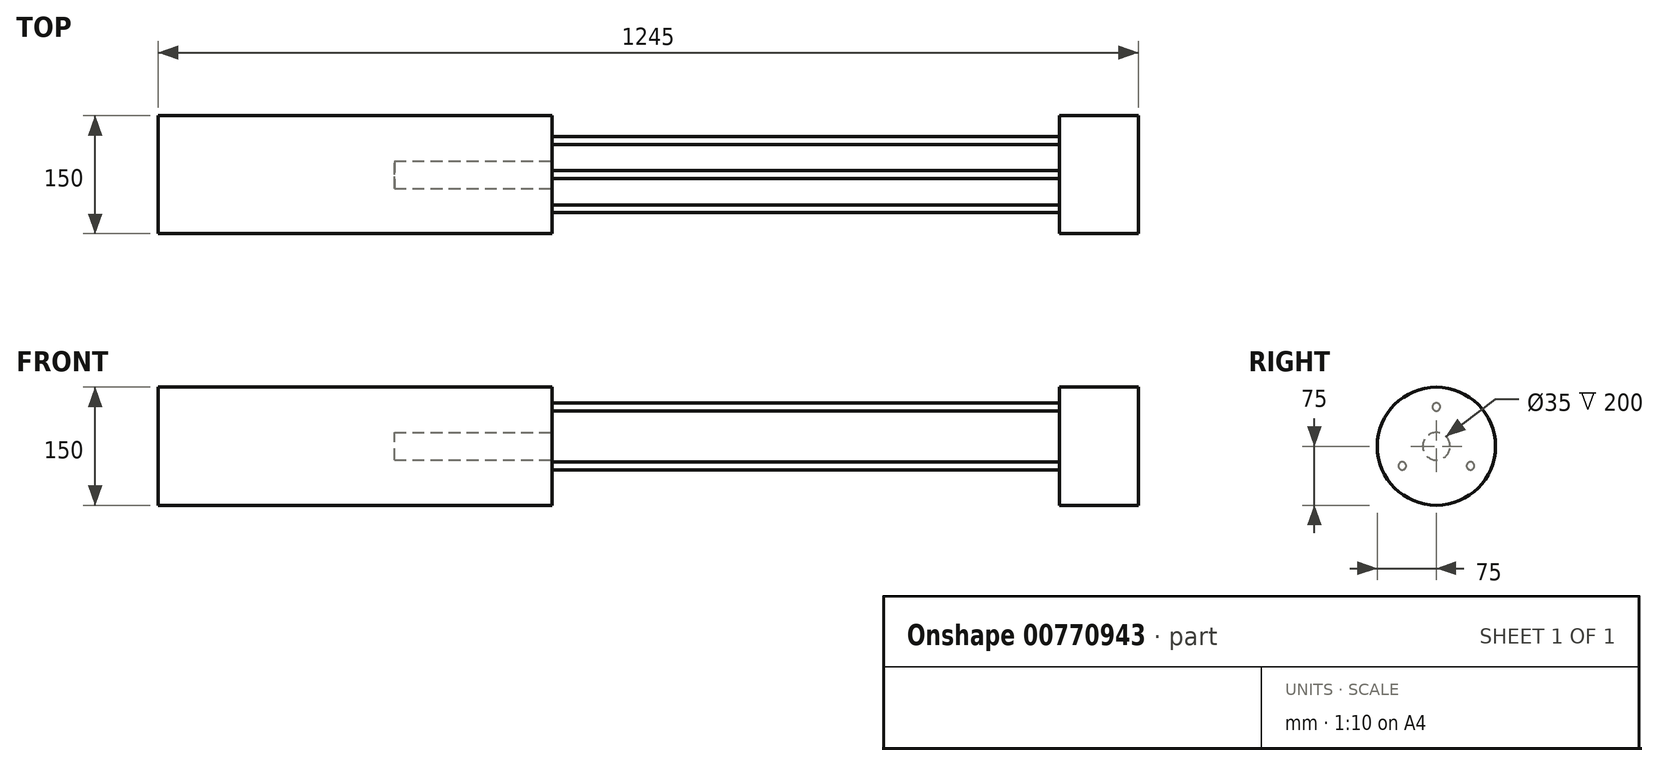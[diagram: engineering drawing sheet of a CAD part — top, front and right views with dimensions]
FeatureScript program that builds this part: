
annotation { "Feature Type Name" : "Feature", "Feature Type Description" : "" }
export const myFeature = defineFeature(function(context is Context, id is Id, definition is map)
    precondition{}
    {
        {
            var Q0;
            Q0=qCreatedBy(makeId("Top.planeOp"),FACE);
            var sketch = newSketch(context, id + "F0", { "sketchPlane" : qUnion([Q0])});
            skLineSegment(sketch, "E0", {"start": v(-500, 0) * mm, "end": v(-500, -75) * mm});
            skLineSegment(sketch, "E1", {"start": v(-500, -75) * mm, "end": v(0, -75) * mm});
            skLineSegment(sketch, "E2", {"start": v(0, -75) * mm, "end": v(0, -17.5) * mm});
            skLineSegment(sketch, "E3", {"start": v(0, -17.5) * mm, "end": v(-200, -17.5) * mm});
            skLineSegment(sketch, "E4", {"start": v(-200, -17.5) * mm, "end": v(-200, 0) * mm});
            skLineSegment(sketch, "E5", {"start": v(-200, 0) * mm, "end": v(-500, 0) * mm});
            skSolve(sketch);
        }
        {
            var Q0;
            Q0=qCreatedBy(makeId("Top.planeOp"),FACE);
            var sketch = newSketch(context, id + "F1", { "sketchPlane" : qUnion([Q0])});
            skLineSegment(sketch, "E6.bottom", {"start": v(645, -75) * mm, "end": v(745, -75) * mm});
            skLineSegment(sketch, "E6.top", {"start": v(645, 0) * mm, "end": v(745, 0) * mm});
            skLineSegment(sketch, "E6.left", {"start": v(645, -75) * mm, "end": v(645, 0) * mm});
            skLineSegment(sketch, "E6.right", {"start": v(745, -75) * mm, "end": v(745, 0) * mm});
            skSolve(sketch);
        }
        {
            var Q0;
            Q0=makeQuery(id+"F0.imprint","IMPRINT",FACE,{"disambiguationData":[TD([[makeQuery(id+"F0.imprint","IMPRINT",EDGE,{"derivedFrom":sQuery(id+"F0.wireOp",EDGE,"E0")}),1.0]])]});
            var Q1;
            Q1=makeQuery(id+"FkN8uBkjpyCZk5b_23.imprint","IMPRINT",FACE,{"disambiguationData":[TD([[makeQuery(id+"FkN8uBkjpyCZk5b_23.imprint","IMPRINT",EDGE,{"derivedFrom":sQuery(id+"FkN8uBkjpyCZk5b_23.wireOp",EDGE,"00949d21-04e9-4acd-8803-175544acd0f4.4.0.0")}),1.0]])]});
            var Q2;
            Q2=makeQuery(id+"FkN8uBkjpyCZk5b_23.imprint","IMPRINT",FACE,{"disambiguationData":[TD([[makeQuery(id+"FkN8uBkjpyCZk5b_23.imprint","IMPRINT",EDGE,{"derivedFrom":sQuery(id+"FkN8uBkjpyCZk5b_23.wireOp",EDGE,"00949d21-04e9-4acd-8803-175544acd0f4.9.0.0")}),1.0]])]});
            var Q3;
            Q3=makeQuery(id+"FkN8uBkjpyCZk5b_23.imprint","IMPRINT",FACE,{"disambiguationData":[TD([[makeQuery(id+"FkN8uBkjpyCZk5b_23.imprint","IMPRINT",EDGE,{"derivedFrom":sQuery(id+"FkN8uBkjpyCZk5b_23.wireOp",EDGE,"00949d21-04e9-4acd-8803-175544acd0f4.3.0.0")}),1.0]])]});
            var Q4;
            Q4=makeQuery(id+"FkN8uBkjpyCZk5b_23.imprint","IMPRINT",FACE,{"disambiguationData":[TD([[makeQuery(id+"FkN8uBkjpyCZk5b_23.imprint","IMPRINT",EDGE,{"derivedFrom":sQuery(id+"FkN8uBkjpyCZk5b_23.wireOp",EDGE,"00949d21-04e9-4acd-8803-175544acd0f4.2.0.0")}),1.0]])]});
            var Q5;
            Q5=makeQuery(id+"FkN8uBkjpyCZk5b_23.imprint","IMPRINT",FACE,{"disambiguationData":[TD([[makeQuery(id+"FkN8uBkjpyCZk5b_23.imprint","IMPRINT",EDGE,{"derivedFrom":sQuery(id+"FkN8uBkjpyCZk5b_23.wireOp",EDGE,"00949d21-04e9-4acd-8803-175544acd0f4.10.0.0")}),1.0]])]});
            var Q6;
            Q6=makeQuery(id+"FkN8uBkjpyCZk5b_23.imprint","IMPRINT",FACE,{"disambiguationData":[TD([[makeQuery(id+"FkN8uBkjpyCZk5b_23.imprint","IMPRINT",EDGE,{"derivedFrom":sQuery(id+"FkN8uBkjpyCZk5b_23.wireOp",EDGE,"00949d21-04e9-4acd-8803-175544acd0f4.1.0.0")}),1.0]])]});
            var Q7;
            Q7=makeQuery(id+"FkN8uBkjpyCZk5b_23.imprint","IMPRINT",FACE,{"disambiguationData":[TD([[makeQuery(id+"FkN8uBkjpyCZk5b_23.imprint","IMPRINT",EDGE,{"derivedFrom":sQuery(id+"FkN8uBkjpyCZk5b_23.wireOp",EDGE,"00949d21-04e9-4acd-8803-175544acd0f4.8.0.0")}),1.0]])]});
            var Q8;
            Q8=makeQuery(id+"FkN8uBkjpyCZk5b_23.imprint","IMPRINT",FACE,{"disambiguationData":[TD([[makeQuery(id+"FkN8uBkjpyCZk5b_23.imprint","IMPRINT",EDGE,{"derivedFrom":sQuery(id+"FkN8uBkjpyCZk5b_23.wireOp",EDGE,"00949d21-04e9-4acd-8803-175544acd0f4.17.0.0")}),1.0]])]});
            var Q9;
            Q9=makeQuery(id+"FkN8uBkjpyCZk5b_23.imprint","IMPRINT",FACE,{"disambiguationData":[TD([[makeQuery(id+"FkN8uBkjpyCZk5b_23.imprint","IMPRINT",EDGE,{"derivedFrom":sQuery(id+"FkN8uBkjpyCZk5b_23.wireOp",EDGE,"00949d21-04e9-4acd-8803-175544acd0f4.16.0.0")}),1.0]])]});
            var Q10;
            Q10=makeQuery(id+"FkN8uBkjpyCZk5b_23.imprint","IMPRINT",FACE,{"disambiguationData":[TD([[makeQuery(id+"FkN8uBkjpyCZk5b_23.imprint","IMPRINT",EDGE,{"derivedFrom":sQuery(id+"FkN8uBkjpyCZk5b_23.wireOp",EDGE,"00949d21-04e9-4acd-8803-175544acd0f4.12.0.0")}),1.0]])]});
            var Q11;
            Q11=makeQuery(id+"FkN8uBkjpyCZk5b_23.imprint","IMPRINT",FACE,{"disambiguationData":[TD([[makeQuery(id+"FkN8uBkjpyCZk5b_23.imprint","IMPRINT",EDGE,{"derivedFrom":sQuery(id+"FkN8uBkjpyCZk5b_23.wireOp",EDGE,"00949d21-04e9-4acd-8803-175544acd0f4.5.0.0")}),1.0]])]});
            var Q12;
            Q12=makeQuery(id+"FkN8uBkjpyCZk5b_23.imprint","IMPRINT",FACE,{"disambiguationData":[TD([[makeQuery(id+"FkN8uBkjpyCZk5b_23.imprint","IMPRINT",EDGE,{"derivedFrom":sQuery(id+"FkN8uBkjpyCZk5b_23.wireOp",EDGE,"00949d21-04e9-4acd-8803-175544acd0f4.6.0.0")}),1.0]])]});
            var Q13;
            Q13=makeQuery(id+"FkN8uBkjpyCZk5b_23.imprint","IMPRINT",FACE,{"disambiguationData":[TD([[makeQuery(id+"FkN8uBkjpyCZk5b_23.imprint","IMPRINT",EDGE,{"derivedFrom":sQuery(id+"FkN8uBkjpyCZk5b_23.wireOp",EDGE,"00949d21-04e9-4acd-8803-175544acd0f4.11.0.0")}),1.0]])]});
            var Q14;
            Q14=makeQuery(id+"FkN8uBkjpyCZk5b_23.imprint","IMPRINT",FACE,{"disambiguationData":[TD([[makeQuery(id+"FkN8uBkjpyCZk5b_23.imprint","IMPRINT",EDGE,{"derivedFrom":sQuery(id+"FkN8uBkjpyCZk5b_23.wireOp",EDGE,"00949d21-04e9-4acd-8803-175544acd0f4.7.0.0")}),1.0]])]});
            var Q15;
            Q15=makeQuery(id+"FkN8uBkjpyCZk5b_23.imprint","IMPRINT",FACE,{"disambiguationData":[TD([[makeQuery(id+"FkN8uBkjpyCZk5b_23.imprint","IMPRINT",EDGE,{"derivedFrom":sQuery(id+"FkN8uBkjpyCZk5b_23.wireOp",EDGE,"f0441947-bad0-42c7-8f70-0018d09dc495.bottom")}),-1.0]])]});
            var Q16;
            Q16=makeQuery(id+"FkN8uBkjpyCZk5b_23.imprint","IMPRINT",FACE,{"disambiguationData":[TD([[makeQuery(id+"FkN8uBkjpyCZk5b_23.imprint","IMPRINT",EDGE,{"derivedFrom":sQuery(id+"FkN8uBkjpyCZk5b_23.wireOp",EDGE,"00949d21-04e9-4acd-8803-175544acd0f4.14.0.0")}),1.0]])]});
            var Q17;
            Q17=makeQuery(id+"FkN8uBkjpyCZk5b_23.imprint","IMPRINT",FACE,{"disambiguationData":[TD([[makeQuery(id+"FkN8uBkjpyCZk5b_23.imprint","IMPRINT",EDGE,{"derivedFrom":sQuery(id+"FkN8uBkjpyCZk5b_23.wireOp",EDGE,"00949d21-04e9-4acd-8803-175544acd0f4.13.0.0")}),1.0]])]});
            var Q18;
            Q18=makeQuery(id+"F1.imprint","IMPRINT",FACE,{"disambiguationData":[TD([[makeQuery(id+"F1.imprint","IMPRINT",EDGE,{"derivedFrom":sQuery(id+"F1.wireOp",EDGE,"E6.bottom")}),1.0]])]});
            var Q19;
            Q19=makeQuery(id+"FkN8uBkjpyCZk5b_23.imprint","IMPRINT",FACE,{"disambiguationData":[TD([[makeQuery(id+"FkN8uBkjpyCZk5b_23.imprint","IMPRINT",EDGE,{"derivedFrom":sQuery(id+"FkN8uBkjpyCZk5b_23.wireOp",EDGE,"00949d21-04e9-4acd-8803-175544acd0f4.15.0.0")}),1.0]])]});
            var Q20;
            Q20=sQuery(id+"F0.wireOp",EDGE,"E5");
            revolve(context, id + "F2", {"surfaceOperationType" : NewSurfaceOperationType.NEW, "entities" : qUnion([Q0, Q1, Q2, Q3, Q4, Q5, Q6, Q7, Q8, Q9, Q10, Q11, Q12, Q13, Q14, Q15, Q16, Q17, Q18, Q19]), "axis" : qUnion([Q20]), "revolveType" : RevolveType.FULL});
        }
        {
            var Q0;
            Q0=qCreatedBy(makeId("Right.planeOp"),FACE);
            var sketch = newSketch(context, id + "F3", { "sketchPlane" : qUnion([Q0])});
            skCircle(sketch, "E7", {"center": v(0, 50) * mm, "radius": 5 * mm});
            skCircle(sketch, "E8.1.0", {"center": v(-43.3, -25) * mm, "radius": 5 * mm});
            skCircle(sketch, "E8.2.0", {"center": v(43.3, -25) * mm, "radius": 5 * mm});
            skPoint(sketch, "E8.center", {"position": v(0, 0) * mm});
            skSolve(sketch);
        }
        {
            var Q0;
            Q0=qSketchRegion(id+"F3",true);
            var Q1;
            Q1=makeQuery(id+"F2.opRevolve","SWEPT_FACE",FACE,{"disambiguationData":[OSD([sQuery(id+"F1.wireOp",EDGE,"E6.left")])]});
            extrude(context, id + "F4", {"entities" : qUnion([Q0]), "endBound" : BoundingType.UP_TO_SURFACE, "depth" : 25 * mm, "endBoundEntityFace" : qUnion([Q1]), "offsetDistance" : 25 * mm, "offsetOppositeDirection" : true});
        }
    });
